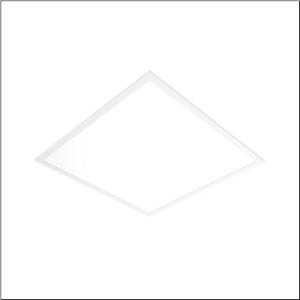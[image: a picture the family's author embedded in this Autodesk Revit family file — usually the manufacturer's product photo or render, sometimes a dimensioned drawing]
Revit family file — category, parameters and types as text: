
# Revit family: apollon_r__41_51mh12w72343_d43e
name_source: partatom
category: Lighting Fixtures
units: mm (PartAtom-declared; Revit-internal decimal feet)

## family parameters
Cut with Voids When Loaded = No
Host = Face
Light Source = No
Part Type = Normal
Room Calculation Point = No
Round Connector Dimension = Use Diameter
Shared = No

## types (1)
- Apollon® 41 (1 x LED, 3500 lm, 28.5 W, 3000K)
    Apparent Load = 29 VA
    CIE Flux Codes = 61 87 97 100 100
    Color Rendering = 80
    Color Temperature = 3000K
    Default Elevation = 1800 mm
    Description = Apollon® 41, office luminaire, primary optical cover: prismatic diffuser, of PS, light emission: direct distribution, primary light characteristic: symmetric, installation type: lay-in mounting, LED, rated luminous flux: 3.500lm, luminous efficacy: 123lm/W, light colour: 830, colour temperature: 3000K, with terminal, 3-pole, mains connection: 220..240V, AC, 50/60Hz, housing, of aluminium section, traffic white (RAL 9016), module: M600, length: 600mm, width: 600mm, height: 28mm, housing upper side, of sheet steel, protection rating (complete): IP20, protection rating (lamp compartment, on room side): IP40, insulation class (complete): insulation class II (safety insulation), certification: CE, ENEC, permissible operating ambient temperature: -25..+40°C, packaging unit: 1 piece
    Height = 0 mm  [stored 0 ft]
    Lamp = 1 x LED
    Lamp Light Flux = 3500 lm
    Lamp Power = 28.5 W
    Lamp count = 1
    Length = 600 mm
    Luminous efficacy = 123 lm/W
    Manufacturer = Siteco
    ModVariant = No
    Model = 51MH12W72343
    Mounting Place = Ceiling
    Mounting Type = Recessed
    Number of Poles = 1
    OnlyDefault = Yes
    Power Factor = 1
    Product Name = Apollon® 41
    Product group = office luminaire | ceiling recessed
    ProductGroupID = 401
    Protection Class = Protection class II
    Protection Degree = IP 20
    RLX_Detail_Level = 1
    RLX_Emergency_Light_Flux = 0 lm
    RLX_Emergency_Type = 0
    RLX_Emergency_Type_DB = No
    RlxData = <blob elided: 12181 chars, md5=28848de4>
    Socket = socket
    Standby Power = 0 W
    System Light Flux = 3500 lm
    System Power = 29 W
    Type Comments = Product without accessories
    Type Image = l_1291024.jpg
    URL = http://relux.com
    VarID = ---
    Voltage = 0 V
    Weight = 0.00 kg
    Width = 600 mm

note: [stored X ft] marks values corroborated as IEEE doubles in the binary element streams (Revit-internal decimal feet)

## geometry (parser evidence)
native form markers: Sweep x11
no freeform markers — native parametric forms only
